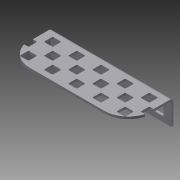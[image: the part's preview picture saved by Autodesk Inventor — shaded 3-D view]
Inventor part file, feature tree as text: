
AUTODESK INVENTOR PART (.ipt)
format: ipt  version: 2012 (Build 160160000, 160)  size: 1,547,776 bytes
history: native  units: in
note: dims shown in document units (in); Inventor stores cm internally (conversion verified against a paired STEP export)
features: sketch x6, plane x2, split x2, fillet x2, other x1, imported_body x1
ambient origin geometry x8: Origin, YZ Plane, XZ Plane, XY Plane, X Axis, Y Axis, Z Axis, Center Point
feature tree (14):
  parser-record x1  (decoder bookkeeping rows leaked as tree rows — omitted from the tree; the rows remain in map.json)
  imported_body  "Base1"
  sketch  "Sketch1"  dims[d0=9.8425in d2=0.5in d3=0.3937in d5=1.0in]
  sketch  "Sketch2"  dims[d7=9.8425in d9=0.5in d10=0.7874in d12=0.5in]
  sketch  "Sketch3"  dims[d15=9.4488in d17=0.5in d18=0.3937in d20=1.0in d25=0.091in d26=-2.5in d27=0.5in]
  sketch  "Sketch4"  dims[d28=0.5in]
  plane  "Work Plane2"
  split  "Split1"
  split  "Split2"
  sketch  "Sketch6"
  sketch  "Sketch7"
  fillet  "Fillet1"  Radius=0.091in
  fillet  "Fillet2"  Radius=0.5in
  plane  "Work Plane1"
